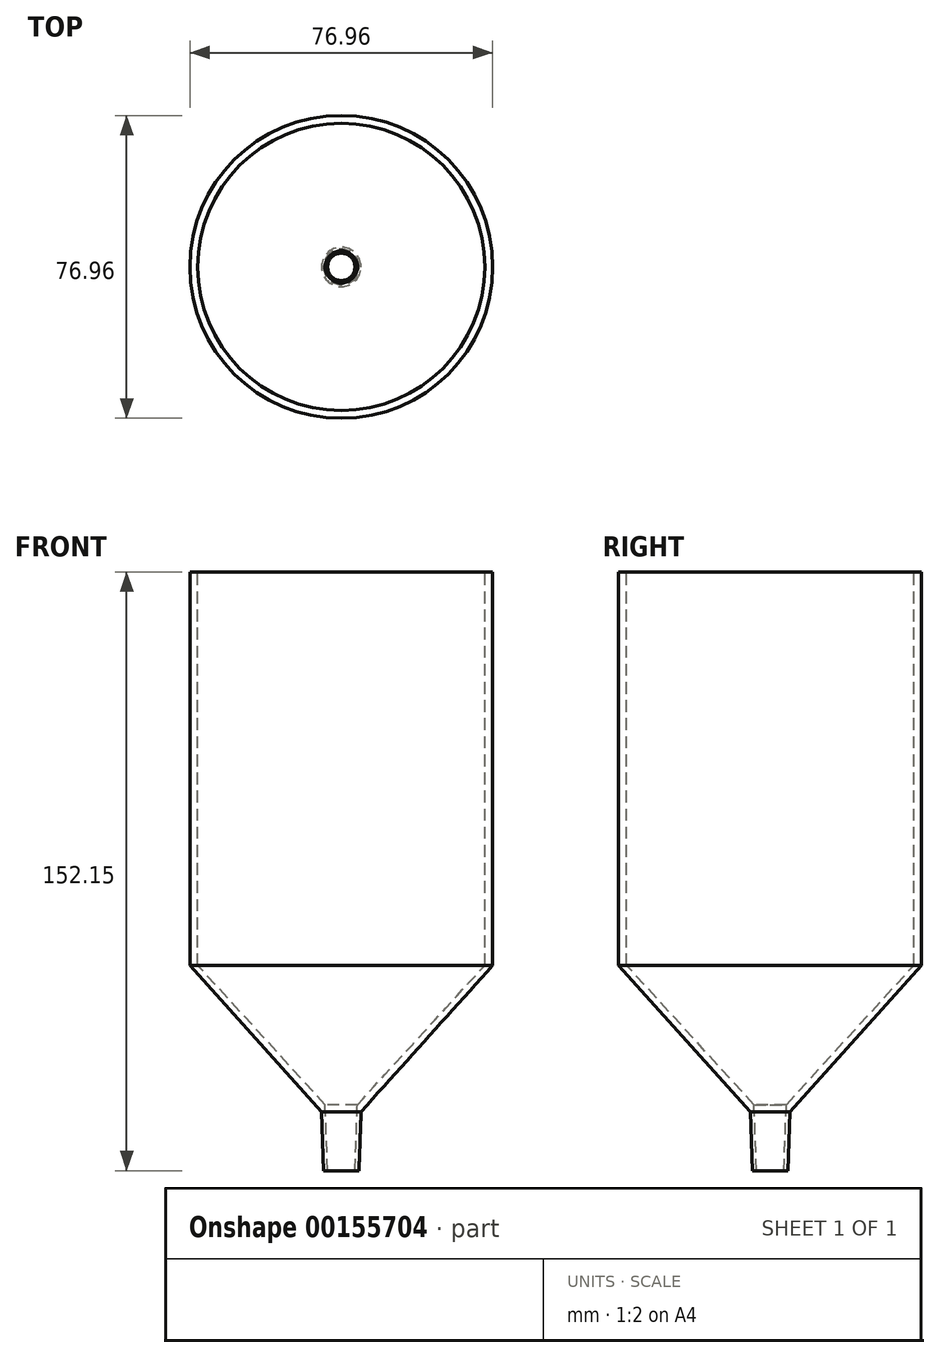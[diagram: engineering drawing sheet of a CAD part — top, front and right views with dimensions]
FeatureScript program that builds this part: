
annotation { "Feature Type Name" : "Feature", "Feature Type Description" : "" }
export const myFeature = defineFeature(function(context is Context, id is Id, definition is map)
    precondition{}
    {
        {
            var Q0;
            Q0=qCreatedBy(makeId("Front.planeOp"),FACE);
            var sketch = newSketch(context, id + "F0", { "sketchPlane" : qUnion([Q0])});
            skLineSegment(sketch, "E0", {"start": v(0, 112.75) * mm, "end": v(0, -14.38) * mm, "construction": true});
            skLineSegment(sketch, "E1", {"start": v(-3.5, 1) * mm, "end": v(-4.5, 1) * mm});
            skLineSegment(sketch, "E2", {"start": v(-4.5, 1) * mm, "end": v(-5.02, 16) * mm});
            skLineSegment(sketch, "E3", {"start": v(-5.02, 16) * mm, "end": v(-38.48, 53.15) * mm});
            skLineSegment(sketch, "E4", {"start": v(-36.48, 53.15) * mm, "end": v(-4.09, 17.76) * mm});
            skLineSegment(sketch, "E5", {"start": v(-4.09, 17.76) * mm, "end": v(-3.5, 1) * mm});
            skLineSegment(sketch, "E6", {"start": v(-38.48, 53.15) * mm, "end": v(-38.48, 153.15) * mm});
            skLineSegment(sketch, "E7", {"start": v(-38.48, 153.15) * mm, "end": v(-36.48, 153.15) * mm});
            skLineSegment(sketch, "E8", {"start": v(-36.48, 153.15) * mm, "end": v(-36.48, 53.15) * mm});
            skSolve(sketch);
        }
        {
            var Q0;
            Q0=makeQuery(id+"F0.imprint","IMPRINT",FACE,{"disambiguationData":[TD([[makeQuery(id+"F0.imprint","IMPRINT",EDGE,{"derivedFrom":sQuery(id+"F0.wireOp",EDGE,"E1")}),-1.0]])]});
            var Q1;
            Q1=sQuery(id+"F0.wireOp",EDGE,"E0");
            revolve(context, id + "F1", {"entities" : qUnion([Q0]), "axis" : qUnion([Q1]), "revolveType" : RevolveType.FULL});
        }
    });
